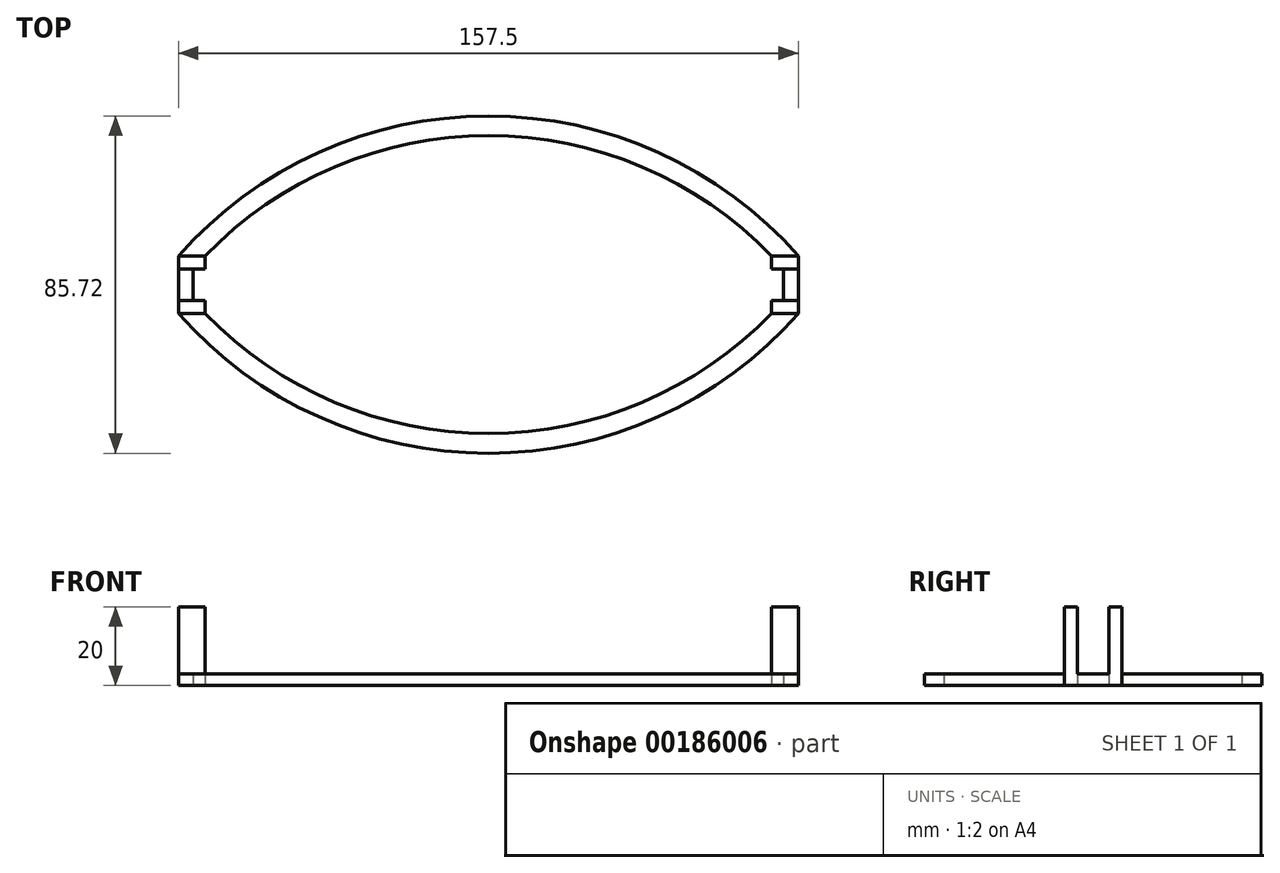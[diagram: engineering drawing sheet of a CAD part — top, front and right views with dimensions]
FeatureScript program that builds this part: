
annotation { "Feature Type Name" : "Feature", "Feature Type Description" : "" }
export const myFeature = defineFeature(function(context is Context, id is Id, definition is map)
    precondition{}
    {
        {
            var Q0;
            Q0=qCreatedBy(makeId("Top.planeOp"),FACE);
            var sketch = newSketch(context, id + "F0", { "sketchPlane" : qUnion([Q0])});
            skLineSegment(sketch, "E0.bottom", {"start": v(0, 0) * mm, "end": v(150, 0) * mm, "construction": true});
            skLineSegment(sketch, "E0.top", {"start": v(0, 8) * mm, "end": v(150, 8) * mm, "construction": true});
            skLineSegment(sketch, "E0.left", {"start": v(0, 0) * mm, "end": v(0, 8) * mm, "construction": true});
            skLineSegment(sketch, "E0.right", {"start": v(150, 0) * mm, "end": v(150, 8) * mm, "construction": true});
            skArc(sketch, "E1", {"start": v(0, 0) * mm, "mid": v(75, -33.86) * mm, "end": v(150, 0) * mm});
            skArc(sketch, "E2", {"start": v(150, 8) * mm, "mid": v(75, 41.86) * mm, "end": v(0, 8) * mm});
            skArc(sketch, "E3.0", {"start": v(153.75, 11.3) * mm, "mid": v(75, 46.86) * mm, "end": v(-3.75, 11.3) * mm});
            skArc(sketch, "E4.0", {"start": v(-3.75, -3.3) * mm, "mid": v(75, -38.86) * mm, "end": v(153.75, -3.3) * mm});
            skLineSegment(sketch, "E5", {"start": v(-3.75, 11.3) * mm, "end": v(-3.75, -3.3) * mm});
            skLineSegment(sketch, "E6", {"start": v(0, 8) * mm, "end": v(0, 0) * mm});
            skLineSegment(sketch, "E7", {"start": v(153.75, 11.3) * mm, "end": v(153.75, -3.3) * mm});
            skLineSegment(sketch, "E8", {"start": v(150, 8) * mm, "end": v(150, 0) * mm});
            skLineSegment(sketch, "E9", {"start": v(153.75, 11.3) * mm, "end": v(146.95, 11.3) * mm});
            skLineSegment(sketch, "E10", {"start": v(153.75, -3.3) * mm, "end": v(146.95, -3.3) * mm});
            skLineSegment(sketch, "E11", {"start": v(-3.75, 11.3) * mm, "end": v(3.05, 11.3) * mm});
            skLineSegment(sketch, "E12", {"start": v(-3.75, -3.3) * mm, "end": v(3.05, -3.3) * mm});
            skLineSegment(sketch, "E13", {"start": v(3.05, 11.3) * mm, "end": v(3.05, 8) * mm});
            skLineSegment(sketch, "E14", {"start": v(3.05, 8) * mm, "end": v(-3.75, 8) * mm});
            skLineSegment(sketch, "E15", {"start": v(3.05, -3.3) * mm, "end": v(3.05, 0) * mm});
            skLineSegment(sketch, "E16", {"start": v(3.05, 0) * mm, "end": v(-3.75, 0) * mm});
            skLineSegment(sketch, "E17", {"start": v(146.95, 11.3) * mm, "end": v(146.95, 8) * mm});
            skLineSegment(sketch, "E18", {"start": v(146.95, 8) * mm, "end": v(153.75, 8) * mm});
            skLineSegment(sketch, "E19", {"start": v(146.95, -3.3) * mm, "end": v(146.95, 0) * mm});
            skLineSegment(sketch, "E20", {"start": v(146.95, 0) * mm, "end": v(153.75, 0) * mm});
            skSolve(sketch);
        }
        {
            var Q0;
            Q0=makeQuery(id+"F0.imprint","IMPRINT",FACE,{"disambiguationData":[TD([[makeQuery(id+"F0.imprint","IMPRINT",EDGE,{"derivedFrom":sQuery(id+"F0.wireOp",EDGE,"E3.0")}),1.0]])]});
            var Q1;
            Q1=makeQuery(id+"F0.imprint","IMPRINT",FACE,{"disambiguationData":[TD([[makeQuery(id+"F0.imprint","IMPRINT",EDGE,{"derivedFrom":sQuery(id+"F0.wireOp",EDGE,"E4.0")}),1.0]])]});
            var Q2;
            {var subQ5=sQuery(id+"F0.wireOp",EDGE,"E8");Q2=makeQuery(id+"F0.imprint","IMPRINT",FACE,{"disambiguationData":[TD([[makeQuery(id+"F0.imprint","IMPRINT",EDGE,{"derivedFrom":subQ5}),1.0]])]});}
            var Q3;
            {var subQ5=sQuery(id+"F0.wireOp",EDGE,"E6");Q3=makeQuery(id+"F0.imprint","IMPRINT",FACE,{"disambiguationData":[TD([[makeQuery(id+"F0.imprint","IMPRINT",EDGE,{"derivedFrom":subQ5}),-1.0]])]});}
            extrude(context, id + "F1", {"entities" : qUnion([Q0, Q1, Q2, Q3]), "depth" : 3 * mm});
        }
        {
            var Q0;
            {var subQ3=sQuery(id+"F0.wireOp",EDGE,"E11");Q0=makeQuery(id+"F0.imprint","IMPRINT",FACE,{"disambiguationData":[TD([[makeQuery(id+"F0.imprint","IMPRINT",EDGE,{"derivedFrom":subQ3}),-1.0]])]});}
            var Q1;
            {var subQ3=sQuery(id+"F0.wireOp",EDGE,"E13");Q1=makeQuery(id+"F0.imprint","IMPRINT",FACE,{"disambiguationData":[TD([[makeQuery(id+"F0.imprint","IMPRINT",EDGE,{"derivedFrom":subQ3}),-1.0]])]});}
            var Q2;
            {var subQ3=sQuery(id+"F0.wireOp",EDGE,"E12");Q2=makeQuery(id+"F0.imprint","IMPRINT",FACE,{"disambiguationData":[TD([[makeQuery(id+"F0.imprint","IMPRINT",EDGE,{"derivedFrom":subQ3}),1.0]])]});}
            var Q3;
            {var subQ3=sQuery(id+"F0.wireOp",EDGE,"E15");Q3=makeQuery(id+"F0.imprint","IMPRINT",FACE,{"disambiguationData":[TD([[makeQuery(id+"F0.imprint","IMPRINT",EDGE,{"derivedFrom":subQ3}),1.0]])]});}
            var Q4;
            {var subQ3=sQuery(id+"F0.wireOp",EDGE,"E9");Q4=makeQuery(id+"F0.imprint","IMPRINT",FACE,{"disambiguationData":[TD([[makeQuery(id+"F0.imprint","IMPRINT",EDGE,{"derivedFrom":subQ3}),1.0]])]});}
            var Q5;
            {var subQ3=sQuery(id+"F0.wireOp",EDGE,"E17");Q5=makeQuery(id+"F0.imprint","IMPRINT",FACE,{"disambiguationData":[TD([[makeQuery(id+"F0.imprint","IMPRINT",EDGE,{"derivedFrom":subQ3}),1.0]])]});}
            var Q6;
            {var subQ3=sQuery(id+"F0.wireOp",EDGE,"E10");Q6=makeQuery(id+"F0.imprint","IMPRINT",FACE,{"disambiguationData":[TD([[makeQuery(id+"F0.imprint","IMPRINT",EDGE,{"derivedFrom":subQ3}),-1.0]])]});}
            var Q7;
            {var subQ3=sQuery(id+"F0.wireOp",EDGE,"E19");Q7=makeQuery(id+"F0.imprint","IMPRINT",FACE,{"disambiguationData":[TD([[makeQuery(id+"F0.imprint","IMPRINT",EDGE,{"derivedFrom":subQ3}),-1.0]])]});}
            extrude(context, id + "F2", {"entities" : qUnion([Q0, Q1, Q2, Q3, Q4, Q5, Q6, Q7]), "operationType" : NewBodyOperationType.ADD, "depth" : 20 * mm});
        }
    });
